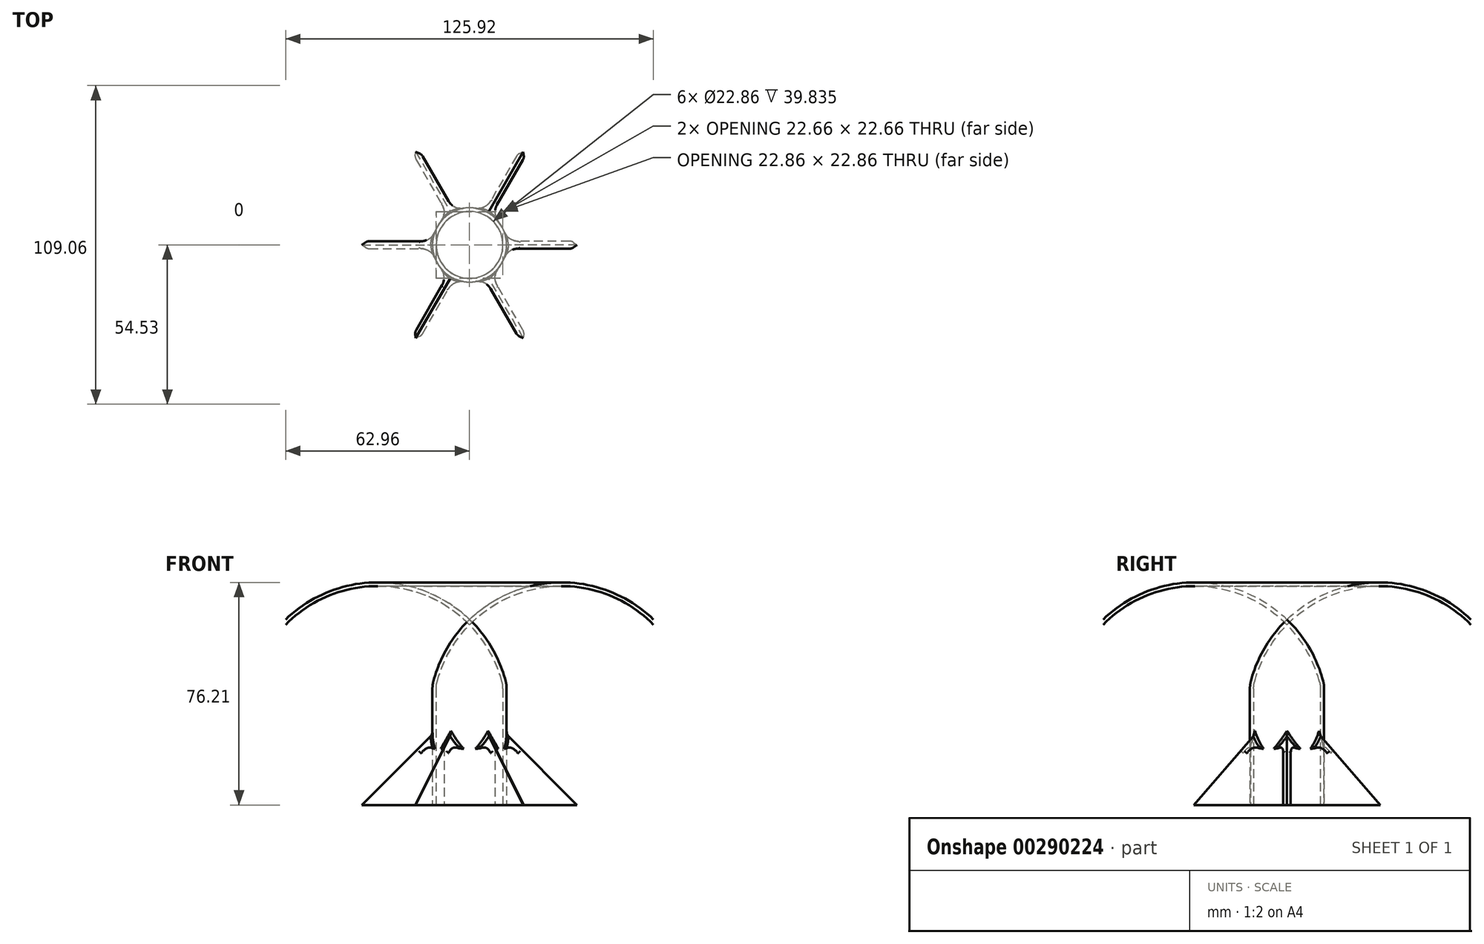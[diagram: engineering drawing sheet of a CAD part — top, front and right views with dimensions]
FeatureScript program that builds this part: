
annotation { "Feature Type Name" : "Feature", "Feature Type Description" : "" }
export const myFeature = defineFeature(function(context is Context, id is Id, definition is map)
    precondition{}
    {
        {
            var Q0;
            Q0=qCreatedBy(makeId("Front.planeOp"),FACE);
            var sketch = newSketch(context, id + "F0", { "sketchPlane" : qUnion([Q0])});
            skLineSegment(sketch, "E0", {"start": v(0, 0) * mm, "end": v(0, 63.5) * mm});
            skArc(sketch, "E1", {"start": v(0, 63.5) * mm, "mid": v(-7.98, 53.2) * mm, "end": v(-12.7, 41.07) * mm});
            skLineSegment(sketch, "E2", {"start": v(-12.7, 41.07) * mm, "end": v(-12.7, 0) * mm});
            skLineSegment(sketch, "E3", {"start": v(-12.7, 0) * mm, "end": v(0, 0) * mm});
            skSolve(sketch);
        }
        {
            var Q0;
            Q0 = qSketchRegion(id + "F0", true);
            var Q1;
            Q1=sQuery(id+"F0.wireOp",EDGE,"E0");
            revolve(context, id + "F1", {"entities" : qUnion([Q0]), "axis" : qUnion([Q1]), "revolveType" : RevolveType.FULL});
        }
        {
            var Q0;
            Q0=makeQuery(id+"F1.opRevolve","SWEPT_EDGE",EDGE,{"disambiguationData":[OSD([sQuery(id+"F0.wireOp",EDGE,"E1"),sQuery(id+"F0.wireOp",EDGE,"E2")])]});
            fillet(context, id + "F2", {"entities" : qUnion([Q0]), "radius" : 10.16 * mm, "tangentPropagation" : true, "allowEdgeOverflow" : false});
        }
        {
            var Q0;
            Q0=makeQuery(id+"F1.opRevolve","SWEPT_FACE",FACE,{"disambiguationData":[OSD([sQuery(id+"F0.wireOp",EDGE,"E3")])]});
            shell(context, id + "F3", {"entities" : qUnion([Q0]), "thickness" : 1.27 * mm});
        }
        {
            var Q0;
            Q0=qCreatedBy(makeId("Front.planeOp"),FACE);
            var sketch = newSketch(context, id + "F4", { "sketchPlane" : qUnion([Q0])});
            skLineSegment(sketch, "E4", {"start": v(-11.43, 0) * mm, "end": v(-11.43, 25.4) * mm});
            skLineSegment(sketch, "E5", {"start": v(-11.43, 25.4) * mm, "end": v(-36.83, 0) * mm});
            skLineSegment(sketch, "E6", {"start": v(-36.83, 0) * mm, "end": v(-11.43, 0) * mm});
            skSolve(sketch);
        }
        {
            var Q0;
            Q0 = qSketchRegion(id + "F4", true);
            extrude(context, id + "F5", {"entities" : qUnion([Q0]), "operationType" : NewBodyOperationType.ADD, "endBound" : BoundingType.SYMMETRIC, "depth" : 2.54 * mm});
        }
        {
            var Q0;
            Q0=makeQuery(id+"F5.opExtrude","CAP_EDGE",EDGE,{"disambiguationData":[OSD([sQuery(id+"F4.wireOp",EDGE,"E5")])],"isStart":false});
            var Q1;
            Q1=makeQuery(id+"F5.opExtrude","CAP_EDGE",EDGE,{"disambiguationData":[OSD([sQuery(id+"F4.wireOp",EDGE,"E5")])],"isStart":true});
            chamfer(context, id + "F6", {"entities" : qUnion([Q0, Q1]), "width" : 1.27 * mm, "tangentPropagation" : true});
        }
        {
            var Q0;
            Q0=makeQuery(id+"F5.boolean.opBoolean","INTERSECT",EDGE,{"derivedFrom":[makeQuery(id+"F1.opRevolve","SWEPT_FACE",FACE,{"disambiguationData":[OSD([sQuery(id+"F0.wireOp",EDGE,"E2")])]}),makeQuery(id+"F5.opExtrude","CAP_FACE",FACE,{"disambiguationData":[OSD([sQuery(id+"F4.wireOp",EDGE,"E4"),sQuery(id+"F4.wireOp",EDGE,"E5"),sQuery(id+"F4.wireOp",EDGE,"E6")])],"isStart":false})]});
            var Q1;
            Q1=makeQuery(id+"F5.boolean.opBoolean","INTERSECT",EDGE,{"derivedFrom":[makeQuery(id+"F1.opRevolve","SWEPT_FACE",FACE,{"disambiguationData":[OSD([sQuery(id+"F0.wireOp",EDGE,"E2")])]}),makeQuery(id+"F5.opExtrude","CAP_FACE",FACE,{"disambiguationData":[OSD([sQuery(id+"F4.wireOp",EDGE,"E4"),sQuery(id+"F4.wireOp",EDGE,"E5"),sQuery(id+"F4.wireOp",EDGE,"E6")])],"isStart":true})]});
            fillet(context, id + "F7", {"entities" : qUnion([Q0, Q1]), "radius" : 5.08 * mm, "tangentPropagation" : true, "allowEdgeOverflow" : false});
        }
        {
            var Q0;
            Q0=makeQuery(id+"F6.opChamfer","BLEND_EDGE",EDGE,{"blendedFrom":[makeQuery(id+"F5.opExtrude","CAP_EDGE",EDGE,{"disambiguationData":[OSD([sQuery(id+"F4.wireOp",EDGE,"E5")])],"isStart":false}),makeQuery(id+"F1.opRevolve","SWEPT_FACE",FACE,{"disambiguationData":[OSD([sQuery(id+"F0.wireOp",EDGE,"E2")])]})],"blendedInto":[makeQuery(id+"F1.opRevolve","SWEPT_FACE",FACE,{"disambiguationData":[OSD([sQuery(id+"F0.wireOp",EDGE,"E2")])]})]});
            var Q1;
            Q1=makeQuery(id+"F6.opChamfer","BLEND_EDGE",EDGE,{"blendedFrom":[makeQuery(id+"F5.opExtrude","CAP_EDGE",EDGE,{"disambiguationData":[OSD([sQuery(id+"F4.wireOp",EDGE,"E5")])],"isStart":true}),makeQuery(id+"F1.opRevolve","SWEPT_FACE",FACE,{"disambiguationData":[OSD([sQuery(id+"F0.wireOp",EDGE,"E2")])]})],"blendedInto":[makeQuery(id+"F1.opRevolve","SWEPT_FACE",FACE,{"disambiguationData":[OSD([sQuery(id+"F0.wireOp",EDGE,"E2")])]})]});
            fillet(context, id + "F8", {"entities" : qUnion([Q0, Q1]), "radius" : 1.27 * mm, "tangentPropagation" : true, "allowEdgeOverflow" : false});
        }
        {
            var Q0;
            {var subQ0=sQuery(id+"F4.wireOp",EDGE,"E5");Q0=makeQuery(id+"F7.opFillet","BLEND_EDGE",EDGE,{"blendedFrom":[makeQuery(id+"F5.boolean.opBoolean","INTERSECT",EDGE,{"derivedFrom":[makeQuery(id+"F1.opRevolve","SWEPT_FACE",FACE,{"disambiguationData":[OSD([sQuery(id+"F0.wireOp",EDGE,"E2")])]}),makeQuery(id+"F5.opExtrude","CAP_FACE",FACE,{"disambiguationData":[OSD([sQuery(id+"F4.wireOp",EDGE,"E4"),subQ0,sQuery(id+"F4.wireOp",EDGE,"E6")])],"isStart":true})]}),makeQuery(id+"F6.opChamfer","BLEND_FACE",FACE,{"disambiguationData":[OSD([subQ0]),TDD([makeQuery(id+"F5.opExtrude","CAP_EDGE",EDGE,{"disambiguationData":[OSD([subQ0])],"isStart":true})])]})],"blendedInto":[makeQuery(id+"F6.opChamfer","BLEND_FACE",FACE,{"disambiguationData":[OSD([subQ0]),TDD([makeQuery(id+"F5.opExtrude","CAP_EDGE",EDGE,{"disambiguationData":[OSD([subQ0])],"isStart":true})])]})]});}
            var Q1;
            {var subQ0=sQuery(id+"F4.wireOp",EDGE,"E5");Q1=makeQuery(id+"F7.opFillet","BLEND_EDGE",EDGE,{"blendedFrom":[makeQuery(id+"F5.boolean.opBoolean","INTERSECT",EDGE,{"derivedFrom":[makeQuery(id+"F1.opRevolve","SWEPT_FACE",FACE,{"disambiguationData":[OSD([sQuery(id+"F0.wireOp",EDGE,"E2")])]}),makeQuery(id+"F5.opExtrude","CAP_FACE",FACE,{"disambiguationData":[OSD([sQuery(id+"F4.wireOp",EDGE,"E4"),subQ0,sQuery(id+"F4.wireOp",EDGE,"E6")])],"isStart":false})]}),makeQuery(id+"F6.opChamfer","BLEND_FACE",FACE,{"disambiguationData":[OSD([subQ0]),TDD([makeQuery(id+"F5.opExtrude","CAP_EDGE",EDGE,{"disambiguationData":[OSD([subQ0])],"isStart":false})])]})],"blendedInto":[makeQuery(id+"F6.opChamfer","BLEND_FACE",FACE,{"disambiguationData":[OSD([subQ0]),TDD([makeQuery(id+"F5.opExtrude","CAP_EDGE",EDGE,{"disambiguationData":[OSD([subQ0])],"isStart":false})])]})]});}
            fillet(context, id + "F9", {"entities" : qUnion([Q0, Q1]), "radius" : 1.27 * mm, "tangentPropagation" : true, "allowEdgeOverflow" : false});
        }
        {
            var Q0;
            Q0=makeQuery(id+"F1.opRevolve","SWEPT_BODY",BODY,{"disambiguationData":[OSD([sQuery(id+"F0.wireOp",EDGE,"E0"),sQuery(id+"F0.wireOp",EDGE,"E1"),sQuery(id+"F0.wireOp",EDGE,"E2"),sQuery(id+"F0.wireOp",EDGE,"E3")])]});
            var Q1;
            {var subQ0=sQuery(id+"F0.wireOp",EDGE,"E1");Q1=makeQuery(id+"F2.opFillet","BLEND_EDGE",EDGE,{"blendedFrom":[makeQuery(id+"F1.opRevolve","SWEPT_EDGE",EDGE,{"disambiguationData":[OSD([subQ0,sQuery(id+"F0.wireOp",EDGE,"E2")])]}),makeQuery(id+"F1.opRevolve","SWEPT_FACE",FACE,{"disambiguationData":[OSD([subQ0])]})],"blendedInto":[makeQuery(id+"F1.opRevolve","SWEPT_FACE",FACE,{"disambiguationData":[OSD([subQ0])]})]});}
            circularPattern(context, id + "F10", {"entities" : qUnion([Q0]), "axis" : qUnion([Q1]), "angle" : 360 * degree, "instanceCount" : 6, "equalSpace" : true});
        }
    });
